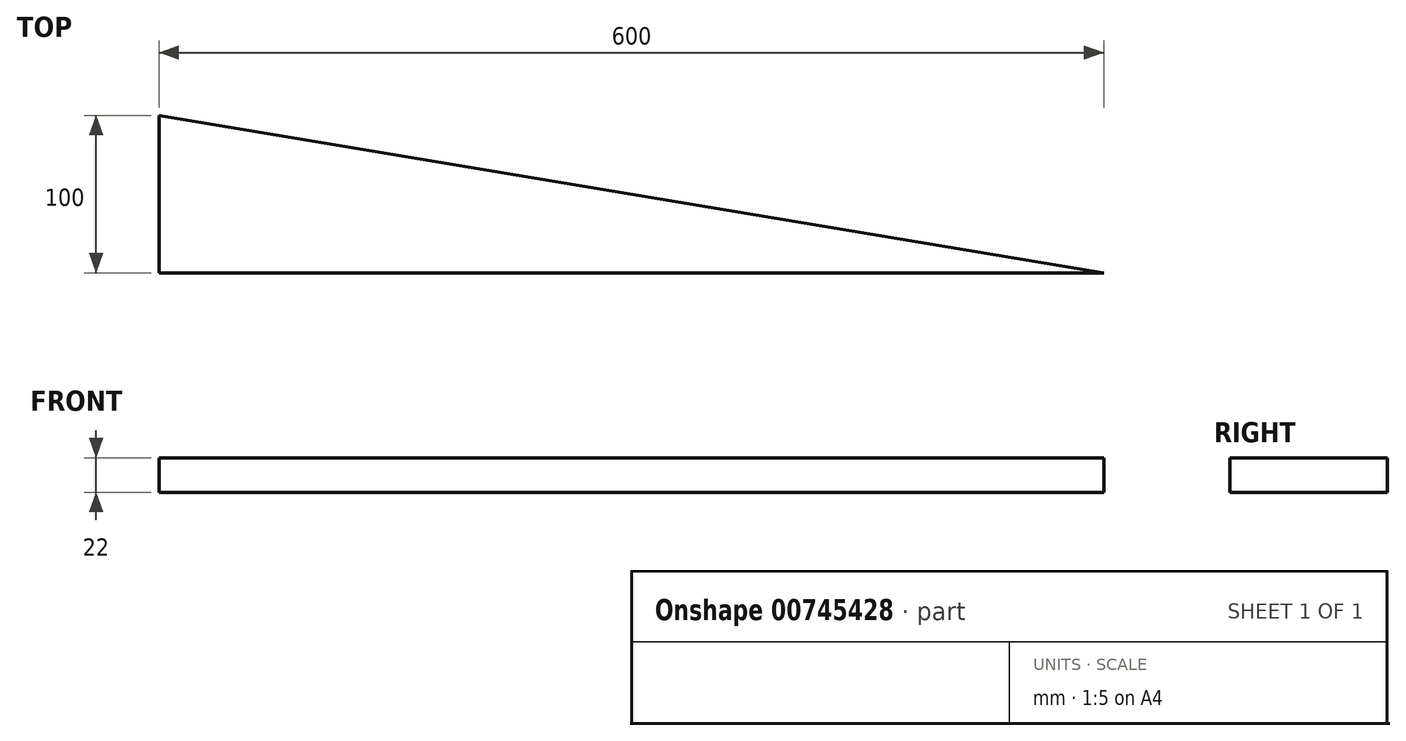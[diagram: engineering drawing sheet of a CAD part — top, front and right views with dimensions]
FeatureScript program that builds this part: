
annotation { "Feature Type Name" : "Feature", "Feature Type Description" : "" }
export const myFeature = defineFeature(function(context is Context, id is Id, definition is map)
    precondition{}
    {
        {
            var Q0;
            Q0=qCreatedBy(makeId("Top.planeOp"),FACE);
            var sketch = newSketch(context, id + "F0", { "sketchPlane" : qUnion([Q0])});
            skLineSegment(sketch, "E0", {"start": v(0, 0) * mm, "end": v(-600, 0) * mm});
            skLineSegment(sketch, "E1", {"start": v(-600, 0) * mm, "end": v(-600, 100) * mm});
            skLineSegment(sketch, "E2", {"start": v(-600, 100) * mm, "end": v(0, 0) * mm});
            skSolve(sketch);
        }
        {
            var Q0;
            Q0=makeQuery(id+"F0.imprint","IMPRINT",FACE,{"disambiguationData":[TD([[makeQuery(id+"F0.imprint","IMPRINT",EDGE,{"derivedFrom":sQuery(id+"F0.wireOp",EDGE,"E0")}),-1.0]])]});
            extrude(context, id + "F1", {"entities" : qUnion([Q0]), "depth" : 22 * mm, "offsetDistance" : 25 * mm});
        }
    });
